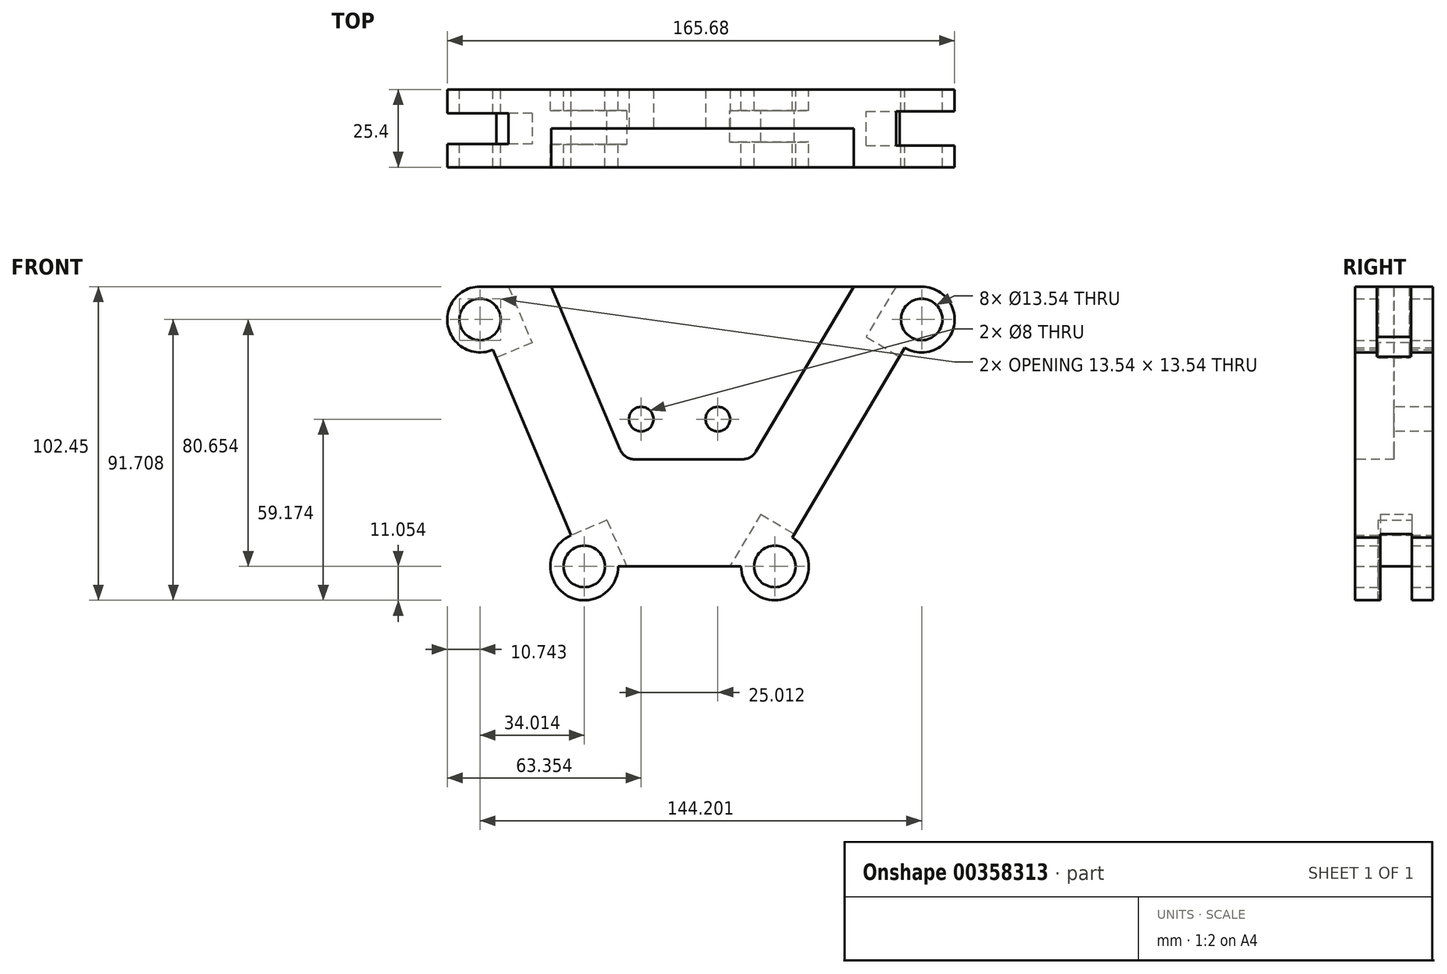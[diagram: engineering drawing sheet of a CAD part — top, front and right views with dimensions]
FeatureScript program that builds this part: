
annotation { "Feature Type Name" : "Feature", "Feature Type Description" : "" }
export const myFeature = defineFeature(function(context is Context, id is Id, definition is map)
    precondition{}
    {
        {
            var Q0;
            Q0=qCreatedBy(makeId("Front.planeOp"),FACE);
            var sketch = newSketch(context, id + "F0", { "sketchPlane" : qUnion([Q0])});
            skPoint(sketch, "E0.middle", {"position": v(0, 0) * mm});
            skCircle(sketch, "E1", {"center": v(-65.12, 45.4) * mm, "radius": 10.74 * mm});
            skCircle(sketch, "E2", {"center": v(79.08, 45.4) * mm, "radius": 10.74 * mm});
            skCircle(sketch, "E3", {"center": v(-65.12, 45.4) * mm, "radius": 6.77 * mm});
            skCircle(sketch, "E4", {"center": v(79.08, 45.4) * mm, "radius": 6.77 * mm});
            skLineSegment(sketch, "E5", {"start": v(-65.12, 45.4) * mm, "end": v(79.08, 45.4) * mm, "construction": true});
            skCircle(sketch, "E6", {"center": v(-31.1, -35.25) * mm, "radius": 11.05 * mm});
            skCircle(sketch, "E7", {"center": v(-31.1, -35.25) * mm, "radius": 6.77 * mm});
            skCircle(sketch, "E8", {"center": v(31.16, -35.25) * mm, "radius": 11.05 * mm});
            skCircle(sketch, "E9", {"center": v(31.16, -35.25) * mm, "radius": 6.77 * mm});
            skLineSegment(sketch, "E10", {"start": v(-65.12, 56.15) * mm, "end": v(79.08, 56.15) * mm});
            skLineSegment(sketch, "E11", {"start": v(-65.12, 45.4) * mm, "end": v(-31.1, -35.25) * mm});
            skLineSegment(sketch, "E12", {"start": v(79.08, 45.4) * mm, "end": v(31.16, -35.25) * mm});
            skLineSegment(sketch, "E13", {"start": v(-31.1, -35.25) * mm, "end": v(31.16, -35.25) * mm});
            skSolve(sketch);
        }
        {
            var Q0;
            Q0 = qSketchRegion(id + "F0", true);
            extrude(context, id + "F1", {"entities" : qUnion([Q0]), "endBound" : BoundingType.SYMMETRIC, "depth" : 25.4 * mm});
        }
        {
            var Q0;
            Q0=makeQuery(id+"F1.opExtrude","CAP_FACE",FACE,{"disambiguationData":[OSD([sQuery(id+"F0.wireOp",EDGE,"E1"),sQuery(id+"F0.wireOp",EDGE,"E2"),sQuery(id+"F0.wireOp",EDGE,"E3"),sQuery(id+"F0.wireOp",EDGE,"E4"),sQuery(id+"F0.wireOp",EDGE,"E6"),sQuery(id+"F0.wireOp",EDGE,"E7"),sQuery(id+"F0.wireOp",EDGE,"E8"),sQuery(id+"F0.wireOp",EDGE,"E9"),sQuery(id+"F0.wireOp",EDGE,"E10"),sQuery(id+"F0.wireOp",EDGE,"E11"),sQuery(id+"F0.wireOp",EDGE,"E12"),sQuery(id+"F0.wireOp",EDGE,"E13")])],"isStart":false});
            var sketch = newSketch(context, id + "F2", { "sketchPlane" : qUnion([Q0])});
            skLineSegment(sketch, "E14", {"start": v(-18.06, -0.25) * mm, "end": v(23.43, -0.25) * mm});
            skLineSegment(sketch, "E15", {"start": v(23.43, -0.25) * mm, "end": v(56.94, 56.15) * mm});
            skLineSegment(sketch, "E16", {"start": v(56.94, 56.15) * mm, "end": v(-41.85, 56.15) * mm});
            skLineSegment(sketch, "E17", {"start": v(-41.85, 56.15) * mm, "end": v(-18.06, -0.25) * mm});
            skSolve(sketch);
        }
        {
            var Q0;
            Q0 = qSketchRegion(id + "F2", true);
            extrude(context, id + "F3", {"entities" : qUnion([Q0]), "operationType" : NewBodyOperationType.REMOVE, "oppositeDirection" : true, "depth" : 12.7 * mm});
        }
        {
            var Q0;
            Q0=makeQuery(id+"F3.boolean.opBoolean","COPY",EDGE,{"derivedFrom":makeQuery(id+"F3.opExtrude","SWEPT_EDGE",EDGE,{"disambiguationData":[OSD([sQuery(id+"F2.wireOp",EDGE,"E14"),sQuery(id+"F2.wireOp",EDGE,"E15")])]})});
            var Q1;
            Q1=makeQuery(id+"F3.boolean.opBoolean","COPY",EDGE,{"derivedFrom":makeQuery(id+"F3.opExtrude","SWEPT_EDGE",EDGE,{"disambiguationData":[OSD([sQuery(id+"F2.wireOp",EDGE,"E14"),sQuery(id+"F2.wireOp",EDGE,"E17")])]})});
            fillet(context, id + "F4", {"entities" : qUnion([Q0, Q1]), "radius" : 5.08 * mm, "tangentPropagation" : true, "allowEdgeOverflow" : false});
        }
        {
            var Q0;
            Q0=makeQuery(id+"F3.boolean.opBoolean","COPY",FACE,{"derivedFrom":makeQuery(id+"F3.opExtrude","CAP_FACE",FACE,{"disambiguationData":[OSD([sQuery(id+"F2.wireOp",EDGE,"E14"),sQuery(id+"F2.wireOp",EDGE,"E15"),sQuery(id+"F2.wireOp",EDGE,"E16"),sQuery(id+"F2.wireOp",EDGE,"E17")])],"isStart":false})});
            var sketch = newSketch(context, id + "F5", { "sketchPlane" : qUnion([Q0])});
            skLineSegment(sketch, "E18", {"start": v(0, 0) * mm, "end": v(0, 41.02) * mm, "construction": true});
            skCircle(sketch, "E19", {"center": v(-12.5, 12.87) * mm, "radius": 4 * mm});
            skCircle(sketch, "E20.MirrorC", {"center": v(12.5, 12.87) * mm, "radius": 4 * mm});
            skSolve(sketch);
        }
        {
            var Q0;
            Q0 = qSketchRegion(id + "F5", true);
            extrude(context, id + "F6", {"entities" : qUnion([Q0]), "operationType" : NewBodyOperationType.REMOVE, "oppositeDirection" : true, "depth" : 25.4 * mm});
        }
        {
            var Q0;
            Q0=makeQuery(id+"F1.opExtrude","SWEPT_FACE",FACE,{"disambiguationData":[OSD([sQuery(id+"F0.wireOp",EDGE,"E12")])]});
            var sketch = newSketch(context, id + "F7", { "sketchPlane" : qUnion([Q0])});
            skLineSegment(sketch, "E21", {"start": v(0, 95.14) * mm, "end": v(0, 25.07) * mm, "construction": true});
            skLineSegment(sketch, "E22", {"start": v(0, 90.08) * mm, "end": v(-5.54, 90.08) * mm, "construction": true});
            skLineSegment(sketch, "E23", {"start": v(-5.54, 90.08) * mm, "end": v(-5.54, 68.7) * mm, "construction": true});
            skLineSegment(sketch, "E24", {"start": v(-5.54, 68.7) * mm, "end": v(0, 68.7) * mm, "construction": true});
            skLineSegment(sketch, "E25.MirrorCS", {"start": v(0, 90.08) * mm, "end": v(5.54, 90.08) * mm, "construction": true});
            skLineSegment(sketch, "E26.MirrorCS", {"start": v(5.54, 90.08) * mm, "end": v(5.54, 68.7) * mm, "construction": true});
            skLineSegment(sketch, "E27.MirrorCS", {"start": v(5.54, 68.7) * mm, "end": v(0, 68.7) * mm, "construction": true});
            skSolve(sketch);
        }
        {
            var Q0;
            {var subQ0=sQuery(id+"F0.wireOp",EDGE,"E12");Q0=makeQuery(id+"F7.imprint","IMPRINT",FACE,{"disambiguationData":[TD([[makeQuery(id+"F7.imprint","IMPRINT",EDGE,{"derivedFrom":makeQuery(id+"F1.opExtrude","CAP_EDGE",EDGE,{"disambiguationData":[OSD([subQ0])],"isStart":true})}),-1.0]])]});}
            var sketch = newSketch(context, id + "F8", { "sketchPlane" : qUnion([Q0])});
            skLineSegment(sketch, "E28.bottom", {"start": v(-5.54, 89.8) * mm, "end": v(5.54, 89.8) * mm});
            skLineSegment(sketch, "E28.top", {"start": v(-5.54, 68.25) * mm, "end": v(5.54, 68.25) * mm});
            skLineSegment(sketch, "E28.left", {"start": v(-5.54, 89.8) * mm, "end": v(-5.54, 68.25) * mm});
            skLineSegment(sketch, "E28.right", {"start": v(5.54, 89.8) * mm, "end": v(5.54, 68.25) * mm});
            skSolve(sketch);
        }
        {
            var Q0;
            {var subQ0=sQuery(id+"F0.wireOp",EDGE,"E12");Q0=makeQuery(id+"F7.imprint","IMPRINT",FACE,{"disambiguationData":[TD([[makeQuery(id+"F7.imprint","IMPRINT",EDGE,{"derivedFrom":makeQuery(id+"F1.opExtrude","CAP_EDGE",EDGE,{"disambiguationData":[OSD([subQ0])],"isStart":true})}),-1.0]])]});}
            var sketch = newSketch(context, id + "F9", { "sketchPlane" : qUnion([Q0])});
            skLineSegment(sketch, "E29.bottom", {"start": v(-5.6, 91.95) * mm, "end": v(5.52, 91.95) * mm});
            skLineSegment(sketch, "E29.top", {"start": v(-5.6, 65.33) * mm, "end": v(5.52, 65.33) * mm});
            skLineSegment(sketch, "E29.left", {"start": v(-5.6, 91.95) * mm, "end": v(-5.6, 65.33) * mm});
            skLineSegment(sketch, "E29.right", {"start": v(5.52, 91.95) * mm, "end": v(5.52, 65.33) * mm});
            skSolve(sketch);
        }
        {
            var Q0;
            Q0 = qSketchRegion(id + "F9", true);
            extrude(context, id + "F10", {"entities" : qUnion([Q0]), "operationType" : NewBodyOperationType.REMOVE, "endBound" : BoundingType.SYMMETRIC, "oppositeDirection" : true, "depth" : 25.4 * mm});
        }
        {
            var Q0;
            {var subQ1=sQuery(id+"F8.wireOp",EDGE,"E28.top");Q0=makeQuery(id+"F8.imprint","IMPRINT",FACE,{"disambiguationData":[TD([[makeQuery(id+"F8.imprint","IMPRINT",EDGE,{"derivedFrom":subQ1}),-1.0]])]});}
            var sketch = newSketch(context, id + "F11", { "sketchPlane" : qUnion([Q0])});
            skLineSegment(sketch, "E30.bottom", {"start": v(-4.5, -2) * mm, "end": v(5.74, -2) * mm});
            skLineSegment(sketch, "E30.top", {"start": v(-4.5, -33.05) * mm, "end": v(5.74, -33.05) * mm});
            skLineSegment(sketch, "E30.left", {"start": v(-4.5, -2) * mm, "end": v(-4.5, -33.05) * mm});
            skLineSegment(sketch, "E30.right", {"start": v(5.74, -2) * mm, "end": v(5.74, -33.05) * mm});
            skSolve(sketch);
        }
        {
            var Q0;
            Q0 = qSketchRegion(id + "F11", true);
            extrude(context, id + "F12", {"entities" : qUnion([Q0]), "operationType" : NewBodyOperationType.REMOVE, "endBound" : BoundingType.SYMMETRIC, "oppositeDirection" : true, "depth" : 25.4 * mm});
        }
        {
            var Q0;
            Q0=makeQuery(id+"F1.opExtrude","SWEPT_FACE",FACE,{"disambiguationData":[OSD([sQuery(id+"F0.wireOp",EDGE,"E11")])]});
            var sketch = newSketch(context, id + "F13", { "sketchPlane" : qUnion([Q0])});
            skLineSegment(sketch, "E31.bottom", {"start": v(-4.97, 79.33) * mm, "end": v(5.12, 79.33) * mm});
            skLineSegment(sketch, "E31.top", {"start": v(-4.97, 53.56) * mm, "end": v(5.12, 53.56) * mm});
            skLineSegment(sketch, "E31.left", {"start": v(-4.97, 79.33) * mm, "end": v(-4.97, 53.56) * mm});
            skLineSegment(sketch, "E31.right", {"start": v(5.12, 79.33) * mm, "end": v(5.12, 53.56) * mm});
            skSolve(sketch);
        }
        {
            var Q0;
            Q0 = qSketchRegion(id + "F13", true);
            extrude(context, id + "F14", {"entities" : qUnion([Q0]), "operationType" : NewBodyOperationType.REMOVE, "endBound" : BoundingType.SYMMETRIC, "oppositeDirection" : true, "depth" : 25.4 * mm});
        }
        {
            var Q0;
            Q0=makeQuery(id+"F1.opExtrude","SWEPT_FACE",FACE,{"disambiguationData":[OSD([sQuery(id+"F0.wireOp",EDGE,"E11")])]});
            var sketch = newSketch(context, id + "F15", { "sketchPlane" : qUnion([Q0])});
            skLineSegment(sketch, "E32.bottom", {"start": v(-5.74, -9.34) * mm, "end": v(5.28, -9.34) * mm});
            skLineSegment(sketch, "E32.top", {"start": v(-5.74, -33.66) * mm, "end": v(5.28, -33.66) * mm});
            skLineSegment(sketch, "E32.left", {"start": v(-5.74, -9.34) * mm, "end": v(-5.74, -33.66) * mm});
            skLineSegment(sketch, "E32.right", {"start": v(5.28, -9.34) * mm, "end": v(5.28, -33.66) * mm});
            skSolve(sketch);
        }
        {
            var Q0;
            Q0 = qSketchRegion(id + "F15", true);
            extrude(context, id + "F16", {"entities" : qUnion([Q0]), "operationType" : NewBodyOperationType.REMOVE, "endBound" : BoundingType.SYMMETRIC, "oppositeDirection" : true, "depth" : 25.4 * mm});
        }
    });
